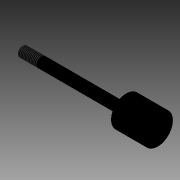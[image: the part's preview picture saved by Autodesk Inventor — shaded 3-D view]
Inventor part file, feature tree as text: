
AUTODESK INVENTOR PART (.ipt)
format: ipt  version: 2014 SP2 (Build 180246200, 246)  size: 145,920 bytes
history: native  units: in
note: dims shown in document units (in); Inventor stores cm internally (conversion verified against a paired STEP export)
features: other x91, revolve x3, sketch x3, thread x1
ambient origin geometry x8: Origin, YZ Plane, XZ Plane, XY Plane, X Axis, Y Axis, Z Axis, Center Point
bodies: Solid1 (feature_tree)
feature tree (98):
  revolve  "Revolution1"  Angle=360.0deg
  revolve  "Revolution2"  Angle=360.0deg
  thread  "Thread1"  [1 undecoded]
  revolve  "Revolution3"  [1 undecoded]
  other  "dia1_XY"
  other  "dia1_YZ"
  other  "dia1_ZX"
  other  "dia1_X"
  other  "dia1_Y"
  other  "dia1_Z"
  other  "dia1_Center"
  other  "dia12_XY"
  other  "dia12_YZ"
  other  "dia12_ZX"
  other  "dia12_X"
  other  "dia12_Y"
  other  "dia12_Z"
  other  "dia12_Center"
  other  "dia1r_XY"
  other  "dia1r_YZ"
  other  "dia1r_ZX"
  other  "dia1r_X"
  other  "dia1r_Y"
  other  "dia1r_Z"
  other  "dia1r_Center"
  other  "dia2_XY"
  other  "dia2_YZ"
  other  "dia2_ZX"
  other  "dia2_X"
  other  "dia2_Y"
  other  "dia2_Z"
  other  "dia2_Center"
  other  "dia22_XY"
  other  "dia22_YZ"
  other  "dia22_ZX"
  other  "dia22_X"
  other  "dia22_Y"
  other  "dia22_Z"
  other  "dia22_Center"
  other  "dia2r_XY"
  other  "dia2r_YZ"
  other  "dia2r_ZX"
  other  "dia2r_X"
  other  "dia2r_Y"
  other  "dia2r_Z"
  other  "dia2r_Center"
  other  "rl1_XY"
  other  "rl1_YZ"
  other  "rl1_ZX"
  other  "rl1_X"
  other  "rl1_Y"
  other  "rl1_Z"
  other  "rl1_Center"
  other  "rl2_XY"
  other  "rl2_YZ"
  other  "rl2_ZX"
  other  "rl2_X"
  other  "rl2_Y"
  other  "rl2_Z"
  other  "rl2_Center"
  other  "rod_cp_XY"
  other  "rod_cp_YZ"
  other  "rod_cp_ZX"
  other  "rod_cp_X"
  other  "rod_cp_Y"
  other  "rod_cp_Z"
  other  "rod_cp_Center"
  other  "stroke1_XY"
  other  "stroke1_YZ"
  other  "stroke1_ZX"
  other  "stroke1_X"
  other  "stroke1_Y"
  other  "stroke1_Z"
  other  "stroke1_Center"
  other  "thd1_XY"
  other  "thd1_YZ"
  other  "thd1_ZX"
  other  "thd1_X"
  other  "thd1_Y"
  other  "thd1_Z"
  other  "thd1_Center"
  other  "thd2_XY"
  other  "thd2_YZ"
  other  "thd2_ZX"
  other  "thd2_X"
  other  "thd2_Y"
  other  "thd2_Z"
  other  "thd2_Center"
  other  "to_rod_clevis_XY"
  other  "to_rod_clevis_YZ"
  other  "to_rod_clevis_ZX"
  other  "to_rod_clevis_X"
  other  "to_rod_clevis_Y"
  other  "to_rod_clevis_Z"
  other  "to_rod_clevis_Center"
  sketch  "Sketch_1"  dims[d0=360.0deg d1=360.0deg]
  sketch  "Sketch_3"  dims[d2=0.4787in d3=0.0in d4=360.0deg]
  sketch  "Sketch_30"  dims[d5=0.0in d6=0.0in d7=0.0in d8=0.0in d9=0.0in d10=0.0in]
note: 2 required parameter values undecoded (feature->parameter linkage not recoverable at this tier; creation-order binding heuristic only, values carry confidence <= 0.55)
